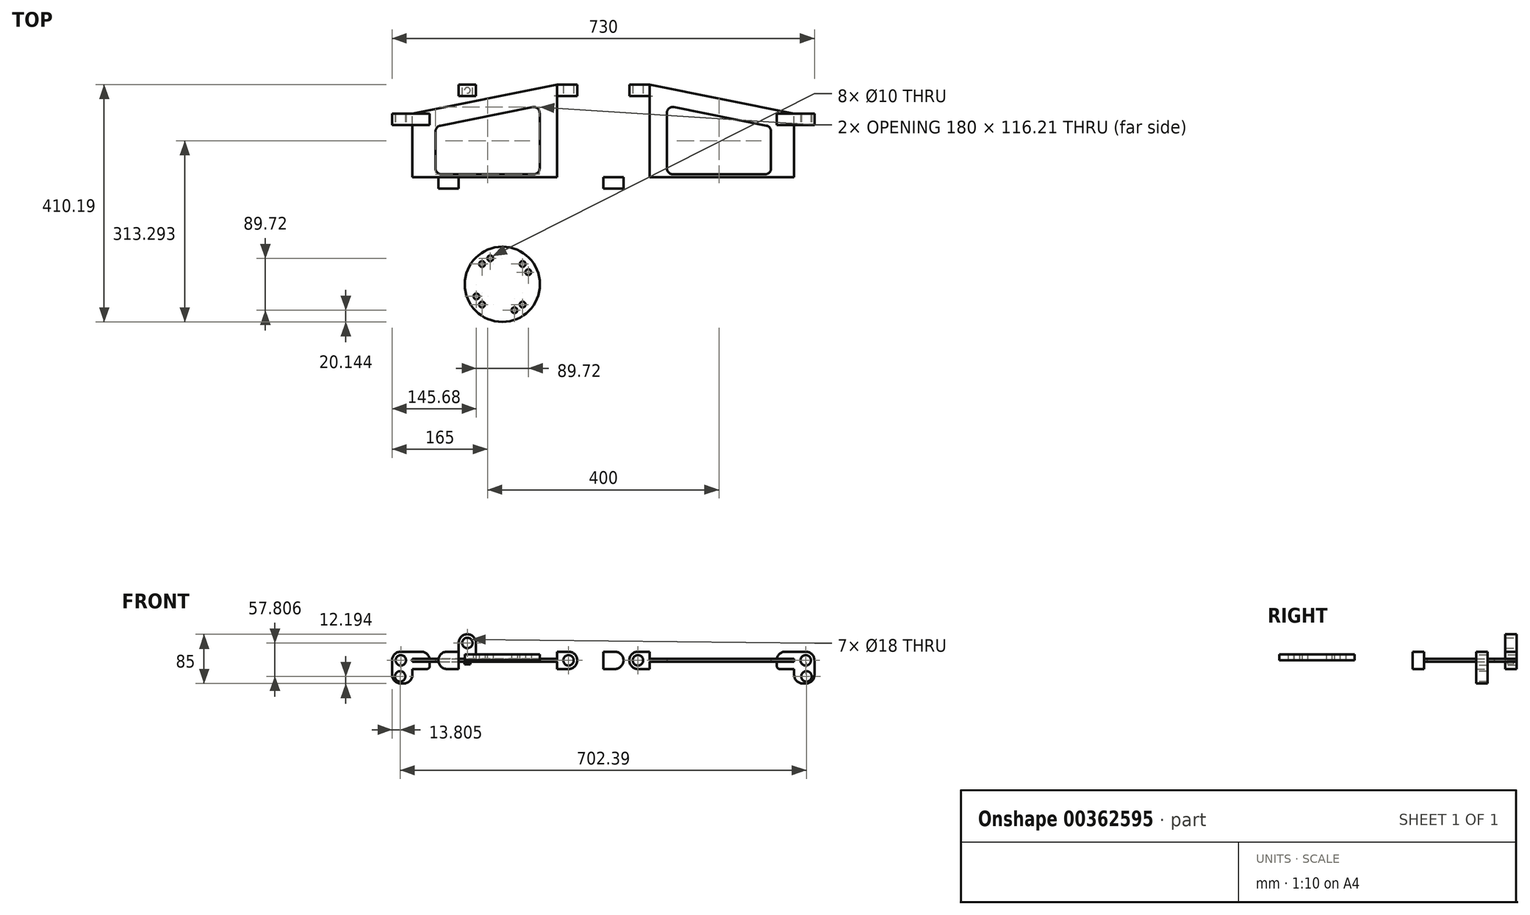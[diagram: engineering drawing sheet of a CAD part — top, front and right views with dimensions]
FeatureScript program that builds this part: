
annotation { "Feature Type Name" : "Feature", "Feature Type Description" : "" }
export const myFeature = defineFeature(function(context is Context, id is Id, definition is map)
    precondition{}
    {
        {
            var Q0;
            Q0=qCreatedBy(makeId("Top.planeOp"),FACE);
            var sketch = newSketch(context, id + "F0", { "sketchPlane" : qUnion([Q0])});
            skLineSegment(sketch, "E0", {"start": v(0, 0) * mm, "end": v(-250, -50) * mm});
            skLineSegment(sketch, "E1", {"start": v(-250, -180) * mm, "end": v(0, -180) * mm});
            skLineSegment(sketch, "E2", {"start": v(0, -180) * mm, "end": v(0, 0) * mm});
            skLineSegment(sketch, "E3", {"start": v(-30, -48.8) * mm, "end": v(-30, -145) * mm});
            skLineSegment(sketch, "E4", {"start": v(-201.96, -70.99) * mm, "end": v(-41.96, -38.99) * mm});
            skLineSegment(sketch, "E5", {"start": v(-200, -155) * mm, "end": v(-40, -155) * mm});
            skPoint(sketch, "E6.visualSharp", {"position": v(-30, -36.6) * mm});
            skArc(sketch, "E6.filletArc", {"start": v(-30, -48.8) * mm, "mid": v(-33.66, -41.06) * mm, "end": v(-41.96, -38.99) * mm});
            skPoint(sketch, "E7.visualSharp", {"position": v(-30, -155) * mm});
            skArc(sketch, "E8.filletArc", {"start": v(-40, -155) * mm, "mid": v(-32.93, -152.07) * mm, "end": v(-30, -145) * mm});
            skLineSegment(sketch, "E9", {"start": v(-250, -180) * mm, "end": v(-250, -50) * mm});
            skLineSegment(sketch, "E10", {"start": v(-210, -80.8) * mm, "end": v(-210, -145) * mm});
            skPoint(sketch, "E11.visualSharp", {"position": v(-210, -72.6) * mm});
            skArc(sketch, "E11.filletArc", {"start": v(-201.96, -70.99) * mm, "mid": v(-207.73, -74.45) * mm, "end": v(-210, -80.8) * mm});
            skLineSegment(sketch, "E12.bottom", {"start": v(-285, -180) * mm, "end": v(0, -180) * mm});
            skLineSegment(sketch, "E12.top", {"start": v(-285, -160) * mm, "end": v(0, -160) * mm});
            skLineSegment(sketch, "E12.left", {"start": v(-285, -180) * mm, "end": v(-285, -160) * mm});
            skLineSegment(sketch, "E12.right", {"start": v(0, -180) * mm, "end": v(0, -160) * mm});
            skLineSegment(sketch, "E13.bottom", {"start": v(-285, -50) * mm, "end": v(-220, -50) * mm});
            skLineSegment(sketch, "E13.top", {"start": v(-285, -70) * mm, "end": v(-220, -70) * mm});
            skLineSegment(sketch, "E13.left", {"start": v(-220, -50) * mm, "end": v(-220, -70) * mm});
            skLineSegment(sketch, "E13.right", {"start": v(-285, -50) * mm, "end": v(-285, -70) * mm});
            skPoint(sketch, "E14.visualSharp", {"position": v(-210, -155) * mm});
            skArc(sketch, "E14.filletArc", {"start": v(-210, -145) * mm, "mid": v(-207.07, -152.07) * mm, "end": v(-200, -155) * mm});
            skLineSegment(sketch, "E15.bottom", {"start": v(-250, 0) * mm, "end": v(-220, 0) * mm});
            skLineSegment(sketch, "E15.top", {"start": v(-250, -20) * mm, "end": v(-220, -20) * mm});
            skLineSegment(sketch, "E15.left", {"start": v(-250, 0) * mm, "end": v(-250, -20) * mm});
            skLineSegment(sketch, "E15.right", {"start": v(-220, 0) * mm, "end": v(-220, -20) * mm});
            skCircle(sketch, "E16", {"center": v(-235, -10) * mm, "radius": 5 * mm});
            skPoint(sketch, "E16.centerSnap0", {"position": v(-235, 0) * mm});
            skPoint(sketch, "E16.centerSnap1", {"position": v(-250, -10) * mm});
            skLineSegment(sketch, "E17.bottom", {"start": v(0, 0) * mm, "end": v(35, 0) * mm});
            skLineSegment(sketch, "E17.top", {"start": v(0, -20) * mm, "end": v(35, -20) * mm});
            skLineSegment(sketch, "E17.left", {"start": v(0, 0) * mm, "end": v(0, -20) * mm});
            skLineSegment(sketch, "E17.right", {"start": v(35, 0) * mm, "end": v(35, -20) * mm});
            skLineSegment(sketch, "E18.bottom", {"start": v(0, -180) * mm, "end": v(35, -180) * mm});
            skLineSegment(sketch, "E18.top", {"start": v(0, -160) * mm, "end": v(35, -160) * mm});
            skLineSegment(sketch, "E18.right", {"start": v(35, -180) * mm, "end": v(35, -160) * mm});
            skPoint(sketch, "E19.center", {"position": v(0, 0) * mm});
            skLineSegment(sketch, "E20.bottom", {"start": v(-129.6, -324.27) * mm, "end": v(-153.54, -390.05) * mm});
            skLineSegment(sketch, "E20.top", {"start": v(-195.38, -300.33) * mm, "end": v(-219.32, -366.1) * mm});
            skLineSegment(sketch, "E20.left", {"start": v(-129.6, -324.27) * mm, "end": v(-195.38, -300.33) * mm});
            skLineSegment(sketch, "E20.right", {"start": v(-153.54, -390.05) * mm, "end": v(-219.32, -366.1) * mm});
            skPoint(sketch, "E20.middle", {"position": v(-174.46, -345.19) * mm});
            skLineSegment(sketch, "E21.bottom", {"start": v(-139.46, -380.19) * mm, "end": v(-209.46, -380.19) * mm});
            skLineSegment(sketch, "E21.top", {"start": v(-139.46, -310.19) * mm, "end": v(-209.46, -310.19) * mm});
            skLineSegment(sketch, "E21.left", {"start": v(-139.46, -380.19) * mm, "end": v(-139.46, -310.19) * mm});
            skLineSegment(sketch, "E21.right", {"start": v(-209.46, -380.19) * mm, "end": v(-209.46, -310.19) * mm});
            skCircle(sketch, "E22", {"center": v(-174.46, -345.19) * mm, "radius": 65 * mm});
            skSolve(sketch);
        }
        {
            var Q0;
            {var subQ5=sQuery(id+"F0.wireOp",EDGE,"uvv03KWO-y48Y-yNLP-V4s5-E3iikQRzJ4Xf.right");Q0=makeQuery(id+"F0.imprint","IMPRINT",FACE,{"disambiguationData":[TD([[makeQuery(id+"F0.imprint","IMPRINT",EDGE,{"derivedFrom":subQ5}),1.0]])]});}
            var Q1;
            {var subQ0=sQuery(id+"F0.wireOp",EDGE,"1lGGe1Tg-SVZ4-Wade-i1KE-bgS1X0YdLzeq");var subQ1=makeQuery(id+"F0.imprint","INTERSECT",VERTEX,{"derivedFrom":[sQuery(id+"F0.wireOp",EDGE,"E0"),subQ0]});Q1=makeQuery(id+"F0.imprint","IMPRINT",FACE,{"disambiguationData":[TD([[makeQuery(id+"F0.imprint","IMPRINT",EDGE,{"disambiguationData":[TD([[subQ1,-1.0]])],"derivedFrom":subQ0}),1.0]])]});}
            var Q2;
            Q2=makeQuery(id+"F0.imprint","IMPRINT",FACE,{"disambiguationData":[TD([[makeQuery(id+"F0.imprint","IMPRINT",EDGE,{"derivedFrom":sQuery(id+"F0.wireOp",EDGE,"uvv03KWO-y48Y-yNLP-V4s5-E3iikQRzJ4Xf.bottom")}),-1.0]])]});
            var Q3;
            {var subQ0=sQuery(id+"F0.wireOp",EDGE,"uvv03KWO-y48Y-yNLP-V4s5-E3iikQRzJ4Xf.bottom");Q3=makeQuery(id+"F0.imprint","IMPRINT",FACE,{"disambiguationData":[TD([[makeQuery(id+"F0.imprint","IMPRINT",EDGE,{"derivedFrom":subQ0}),1.0]])]});}
            var Q4;
            Q4=makeQuery(id+"F0.imprint","IMPRINT",FACE,{"disambiguationData":[TD([[makeQuery(id+"F0.imprint","IMPRINT",EDGE,{"derivedFrom":sQuery(id+"F0.wireOp",EDGE,"0rv8Ym2q-hSoq-A4tP-6C1V-qJVH6aPOWYIx.bottom")}),1.0]])]});
            var Q5;
            Q5=makeQuery(id+"F0.imprint","IMPRINT",FACE,{"disambiguationData":[TD([[makeQuery(id+"F0.imprint","IMPRINT",EDGE,{"derivedFrom":sQuery(id+"F0.wireOp",EDGE,"E13.bottom")}),-1.0]])]});
            var Q6;
            Q6=makeQuery(id+"F0.imprint","IMPRINT",FACE,{"disambiguationData":[TD([[makeQuery(id+"F0.imprint","IMPRINT",EDGE,{"derivedFrom":sQuery(id+"F0.wireOp",EDGE,"E12.bottom")}),1.0]])]});
            var Q7;
            Q7=makeQuery(id+"F0.imprint","IMPRINT",FACE,{"disambiguationData":[TD([[makeQuery(id+"F0.imprint","IMPRINT",EDGE,{"derivedFrom":sQuery(id+"F0.wireOp",EDGE,"E0")}),1.0]])]});
            extrude(context, id + "F1", {"entities" : qUnion([Q0, Q1, Q2, Q3, Q4, Q5, Q6, Q7]), "endBound" : BoundingType.SYMMETRIC, "depth" : 5 * mm});
        }
        {
            var Q0;
            Q0=makeQuery(id+"F0.imprint","IMPRINT",FACE,{"disambiguationData":[TD([[makeQuery(id+"F0.imprint","IMPRINT",EDGE,{"derivedFrom":sQuery(id+"F0.wireOp",EDGE,"uvv03KWO-y48Y-yNLP-V4s5-E3iikQRzJ4Xf.bottom")}),-1.0]])]});
            var Q1;
            Q1=makeQuery(id+"F0.imprint","IMPRINT",FACE,{"disambiguationData":[TD([[makeQuery(id+"F0.imprint","IMPRINT",EDGE,{"derivedFrom":sQuery(id+"F0.wireOp",EDGE,"0rv8Ym2q-hSoq-A4tP-6C1V-qJVH6aPOWYIx.bottom")}),1.0]])]});
            var Q2;
            Q2=makeQuery(id+"F0.imprint","IMPRINT",FACE,{"disambiguationData":[TD([[makeQuery(id+"F0.imprint","IMPRINT",EDGE,{"derivedFrom":sQuery(id+"F0.wireOp",EDGE,"E17.bottom")}),-1.0]])]});
            var Q3;
            Q3=makeQuery(id+"F0.imprint","IMPRINT",FACE,{"disambiguationData":[TD([[makeQuery(id+"F0.imprint","IMPRINT",EDGE,{"derivedFrom":sQuery(id+"F0.wireOp",EDGE,"E18.bottom")}),1.0]])]});
            extrude(context, id + "F2", {"entities" : qUnion([Q0, Q1, Q2, Q3]), "operationType" : NewBodyOperationType.ADD, "endBound" : BoundingType.SYMMETRIC, "depth" : 30 * mm});
        }
        {
            var Q0;
            Q0=makeQuery(id+"F2.opExtrude","CAP_EDGE",EDGE,{"disambiguationData":[OSD([sQuery(id+"F0.wireOp",EDGE,"E18.right")])],"isStart":false});
            var Q1;
            Q1=makeQuery(id+"F2.opExtrude","CAP_EDGE",EDGE,{"disambiguationData":[OSD([sQuery(id+"F0.wireOp",EDGE,"E18.right")])],"isStart":true});
            var Q2;
            Q2=makeQuery(id+"F2.opExtrude","CAP_EDGE",EDGE,{"disambiguationData":[OSD([sQuery(id+"F0.wireOp",EDGE,"E17.right")])],"isStart":true});
            var Q3;
            Q3=makeQuery(id+"F2.opExtrude","CAP_EDGE",EDGE,{"disambiguationData":[OSD([sQuery(id+"F0.wireOp",EDGE,"E17.right")])],"isStart":false});
            fillet(context, id + "F3", {"entities" : qUnion([Q0, Q1, Q2, Q3]), "radius" : 15 * mm, "tangentPropagation" : true, "allowEdgeOverflow" : false});
        }
        {
            var Q0;
            Q0=makeQuery(id+"F0.imprint","IMPRINT",FACE,{"disambiguationData":[TD([[makeQuery(id+"F0.imprint","IMPRINT",EDGE,{"derivedFrom":sQuery(id+"F0.wireOp",EDGE,"E13.bottom")}),-1.0]])]});
            var Q1;
            Q1=makeQuery(id+"F0.imprint","IMPRINT",FACE,{"disambiguationData":[TD([[makeQuery(id+"F0.imprint","IMPRINT",EDGE,{"derivedFrom":sQuery(id+"F0.wireOp",EDGE,"E12.bottom")}),1.0]])]});
            extrude(context, id + "F4", {"entities" : qUnion([Q0, Q1]), "operationType" : NewBodyOperationType.ADD, "endBound" : BoundingType.SYMMETRIC, "depth" : 30 * mm});
        }
        {
            var Q0;
            Q0=makeQuery(id+"F4.opExtrude","CAP_EDGE",EDGE,{"disambiguationData":[OSD([sQuery(id+"F0.wireOp",EDGE,"E13.left")])],"isStart":false});
            var Q1;
            Q1=makeQuery(id+"F4.opExtrude","CAP_EDGE",EDGE,{"disambiguationData":[OSD([sQuery(id+"F0.wireOp",EDGE,"E13.right")])],"isStart":false});
            var Q2;
            Q2=makeQuery(id+"F4.opExtrude","CAP_EDGE",EDGE,{"disambiguationData":[OSD([sQuery(id+"F0.wireOp",EDGE,"E12.left")])],"isStart":false});
            var Q3;
            Q3=makeQuery(id+"F4.opExtrude","CAP_EDGE",EDGE,{"disambiguationData":[OSD([sQuery(id+"F0.wireOp",EDGE,"E12.right")])],"isStart":false});
            fillet(context, id + "F5", {"entities" : qUnion([Q0, Q1, Q2, Q3]), "radius" : 15 * mm, "tangentPropagation" : true, "allowEdgeOverflow" : false});
        }
        {
            var Q0;
            {var subQ5=sQuery(id+"F0.wireOp",EDGE,"E13.right");Q0=makeQuery(id+"F0.imprint","IMPRINT",FACE,{"disambiguationData":[TD([[makeQuery(id+"F0.imprint","IMPRINT",EDGE,{"derivedFrom":subQ5}),1.0]])]});}
            extrude(context, id + "F6", {"entities" : qUnion([Q0]), "operationType" : NewBodyOperationType.ADD, "oppositeDirection" : true, "depth" : 40 * mm});
        }
        {
            var Q0;
            Q0=makeQuery(id+"F6.opExtrude","CAP_EDGE",EDGE,{"disambiguationData":[OSD([sQuery(id+"F0.wireOp",EDGE,"E12.left")])],"isStart":false});
            var Q1;
            Q1=makeQuery(id+"F6.opExtrude","CAP_EDGE",EDGE,{"disambiguationData":[OSD([sQuery(id+"F0.wireOp",EDGE,"E12.right")])],"isStart":false});
            var Q2;
            Q2=makeQuery(id+"F4.opExtrude","CAP_EDGE",EDGE,{"disambiguationData":[OSD([sQuery(id+"F0.wireOp",EDGE,"E13.right")])],"isStart":true});
            var Q3;
            Q3=makeQuery(id+"F6.opExtrude","CAP_EDGE",EDGE,{"disambiguationData":[OSD([sQuery(id+"F0.wireOp",EDGE,"E9")])],"isStart":false});
            var Q4;
            Q4=makeQuery(id+"F6.opExtrude","CAP_EDGE",EDGE,{"disambiguationData":[OSD([sQuery(id+"F0.wireOp",EDGE,"E13.right")])],"isStart":false});
            var Q5;
            Q5=makeQuery(id+"F4.opExtrude","CAP_EDGE",EDGE,{"disambiguationData":[OSD([sQuery(id+"F0.wireOp",EDGE,"E12.left")])],"isStart":true});
            fillet(context, id + "F7", {"entities" : qUnion([Q0, Q1, Q2, Q3, Q4, Q5]), "radius" : 15 * mm, "tangentPropagation" : true, "allowEdgeOverflow" : false});
        }
        {
            var Q0;
            {var subQ0=sQuery(id+"F0.wireOp",EDGE,"E12.bottom");var subQ1=sQuery(id+"F0.wireOp",EDGE,"0rv8Ym2q-hSoq-A4tP-6C1V-qJVH6aPOWYIx.top");Q0=makeQuery(id+"F4.boolean.opBoolean","MERGE",FACE,{"derivedFrom":[makeQuery(id+"F2.boolean.opBoolean","MERGE",FACE,{"derivedFrom":[makeQuery(id+"F1.opExtrude","SWEPT_FACE",FACE,{"disambiguationData":[OSD([sQuery(id+"F0.wireOp",EDGE,"E1"),subQ1,subQ0])]}),makeQuery(id+"F2.opExtrude","SWEPT_FACE",FACE,{"disambiguationData":[OSD([subQ1])]})]}),makeQuery(id+"F4.opExtrude","SWEPT_FACE",FACE,{"disambiguationData":[OSD([subQ0])]})]});}
            var sketch = newSketch(context, id + "F8", { "sketchPlane" : qUnion([Q0])});
            skPoint(sketch, "E23", {"position": v(-270, 0) * mm});
            skPoint(sketch, "E24", {"position": v(20, 0) * mm});
            skPoint(sketch, "E25", {"position": v(-271.2, -27.8) * mm});
            skSolve(sketch);
        }
        {
            var Q0;
            Q0=sQuery(id+"F8.wireOp",VERTEX,"E23");
            var Q1;
            Q1=sQuery(id+"F8.wireOp",VERTEX,"E25");
            var Q2;
            Q2=sQuery(id+"F8.wireOp",VERTEX,"E24");
            var Q3;
            Q3=makeQuery(id+"F1.opExtrude","SWEPT_BODY",BODY,{"disambiguationData":[OSD([sQuery(id+"F0.wireOp",EDGE,"E0"),sQuery(id+"F0.wireOp",EDGE,"E1"),sQuery(id+"F0.wireOp",EDGE,"E2"),sQuery(id+"F0.wireOp",EDGE,"uvv03KWO-y48Y-yNLP-V4s5-E3iikQRzJ4Xf.top"),sQuery(id+"F0.wireOp",EDGE,"uvv03KWO-y48Y-yNLP-V4s5-E3iikQRzJ4Xf.left"),sQuery(id+"F0.wireOp",EDGE,"0rv8Ym2q-hSoq-A4tP-6C1V-qJVH6aPOWYIx.top"),sQuery(id+"F0.wireOp",EDGE,"0rv8Ym2q-hSoq-A4tP-6C1V-qJVH6aPOWYIx.left"),sQuery(id+"F0.wireOp",EDGE,"E3"),sQuery(id+"F0.wireOp",EDGE,"E4"),sQuery(id+"F0.wireOp",EDGE,"E5"),sQuery(id+"F0.wireOp",EDGE,"E6.filletArc"),sQuery(id+"F0.wireOp",EDGE,"E8.filletArc"),sQuery(id+"F0.wireOp",EDGE,"E9"),sQuery(id+"F0.wireOp",EDGE,"E10"),sQuery(id+"F0.wireOp",EDGE,"E11.filletArc"),sQuery(id+"F0.wireOp",EDGE,"ed4627cc-2027-4385-b44c-b2d2488a9f8e.filletArc"),sQuery(id+"F0.wireOp",EDGE,"E12.bottom"),sQuery(id+"F0.wireOp",EDGE,"E12.left"),sQuery(id+"F0.wireOp",EDGE,"E13.left")])]});
            hole(context, id + "F9", {"style" : HoleStyle.SIMPLE, "endStyle" : HoleEndStyle.THROUGH, "holeDiameter" : 18 * mm, "isTappedThrough" : true, "tappedDepth" : 12 * mm, "tapClearance" : 3, "locations" : qUnion([Q0, Q1, Q2]), "scope" : qUnion([Q3])});
        }
        {
            var Q0;
            Q0=makeQuery(id+"F4.opExtrude","CAP_EDGE",EDGE,{"disambiguationData":[OSD([sQuery(id+"F0.wireOp",EDGE,"E13.left")])],"isStart":true});
            var Q1;
            Q1=makeQuery(id+"F2.opExtrude","CAP_EDGE",EDGE,{"disambiguationData":[OSD([sQuery(id+"F0.wireOp",EDGE,"E17.left")])],"isStart":false});
            var Q2;
            Q2=makeQuery(id+"F2.opExtrude","CAP_EDGE",EDGE,{"disambiguationData":[OSD([sQuery(id+"F0.wireOp",EDGE,"E17.left")])],"isStart":true});
            var Q3;
            {var subQ0=sQuery(id+"F0.wireOp",EDGE,"E12.right");var subQ1=sQuery(id+"F0.wireOp",EDGE,"E17.left");var subQ2=sQuery(id+"F0.wireOp",EDGE,"E2");Q3=makeQuery(id+"F2.boolean.opBoolean","SPLIT",EDGE,{"disambiguationData":[topologyDisambiguationEdgeConnected([makeQuery(id+"F2.opExtrude","SWEPT_FACE",FACE,{"disambiguationData":[OSD([subQ1])]})])],"derivedFrom":makeQuery(id+"F1.opExtrude","CAP_EDGE",EDGE,{"disambiguationData":[OSD([subQ2,subQ1,subQ0])],"isStart":true})});}
            var Q4;
            {var subQ0=sQuery(id+"F0.wireOp",EDGE,"E12.right");Q4=makeQuery(id+"F6.boolean.opBoolean","INTERSECT",EDGE,{"derivedFrom":[makeQuery(id+"F4.boolean.opBoolean","MERGE",FACE,{"derivedFrom":[makeQuery(id+"F2.opExtrude","CAP_FACE",FACE,{"disambiguationData":[OSD([sQuery(id+"F0.wireOp",EDGE,"E18.bottom"),sQuery(id+"F0.wireOp",EDGE,"E18.top"),subQ0,sQuery(id+"F0.wireOp",EDGE,"E18.right")])],"isStart":true}),makeQuery(id+"F4.opExtrude","CAP_FACE",FACE,{"disambiguationData":[OSD([sQuery(id+"F0.wireOp",EDGE,"E12.bottom"),sQuery(id+"F0.wireOp",EDGE,"E12.top"),sQuery(id+"F0.wireOp",EDGE,"E12.left"),subQ0])],"isStart":true})]}),makeQuery(id+"F6.opExtrude","SWEPT_FACE",FACE,{"disambiguationData":[OSD([sQuery(id+"F0.wireOp",EDGE,"E9")])]})]});}
            var Q5;
            {var subQ0=sQuery(id+"F0.wireOp",EDGE,"E12.right");var subQ1=sQuery(id+"F0.wireOp",EDGE,"E17.left");var subQ2=sQuery(id+"F0.wireOp",EDGE,"E2");Q5=makeQuery(id+"F2.boolean.opBoolean","SPLIT",EDGE,{"disambiguationData":[topologyDisambiguationEdgeConnected([makeQuery(id+"F2.opExtrude","SWEPT_FACE",FACE,{"disambiguationData":[OSD([subQ1])]})])],"derivedFrom":makeQuery(id+"F1.opExtrude","CAP_EDGE",EDGE,{"disambiguationData":[OSD([subQ2,subQ1,subQ0])],"isStart":false})});}
            fillet(context, id + "F10", {"entities" : qUnion([Q0, Q1, Q2, Q3, Q4, Q5]), "radius" : 5 * mm, "tangentPropagation" : true, "allowEdgeOverflow" : false});
        }
        {
            var Q0;
            Q0=makeQuery(id+"F1.opExtrude","CAP_EDGE",EDGE,{"disambiguationData":[OSD([sQuery(id+"F0.wireOp",EDGE,"E5")])],"isStart":false});
            cPoint(context, id + "F11", {"entities" : qUnion([Q0]), "parameter" : 0.5});
        }
        {
            var Q0;
            Q0=makeQuery(id+"F1.opExtrude","SWEPT_BODY",BODY,{"disambiguationData":[OSD([sQuery(id+"F0.wireOp",EDGE,"E0"),sQuery(id+"F0.wireOp",EDGE,"E1"),sQuery(id+"F0.wireOp",EDGE,"E2"),sQuery(id+"F0.wireOp",EDGE,"uvv03KWO-y48Y-yNLP-V4s5-E3iikQRzJ4Xf.top"),sQuery(id+"F0.wireOp",EDGE,"uvv03KWO-y48Y-yNLP-V4s5-E3iikQRzJ4Xf.left"),sQuery(id+"F0.wireOp",EDGE,"0rv8Ym2q-hSoq-A4tP-6C1V-qJVH6aPOWYIx.top"),sQuery(id+"F0.wireOp",EDGE,"0rv8Ym2q-hSoq-A4tP-6C1V-qJVH6aPOWYIx.left"),sQuery(id+"F0.wireOp",EDGE,"E3"),sQuery(id+"F0.wireOp",EDGE,"E4"),sQuery(id+"F0.wireOp",EDGE,"E5"),sQuery(id+"F0.wireOp",EDGE,"E6.filletArc"),sQuery(id+"F0.wireOp",EDGE,"E8.filletArc"),sQuery(id+"F0.wireOp",EDGE,"E9"),sQuery(id+"F0.wireOp",EDGE,"E10"),sQuery(id+"F0.wireOp",EDGE,"E11.filletArc"),sQuery(id+"F0.wireOp",EDGE,"E12.bottom"),sQuery(id+"F0.wireOp",EDGE,"E12.left"),sQuery(id+"F0.wireOp",EDGE,"E13.left"),sQuery(id+"F0.wireOp",EDGE,"E14.filletArc")])]});
            var Q1;
            Q1=makeQuery(id+"F1.opExtrude","CAP_VERTEX",VERTEX,{"disambiguationData":[OSD([sQuery(id+"F0.wireOp",EDGE,"E5"),sQuery(id+"F0.wireOp",EDGE,"E8.filletArc")])],"isStart":false});
            var Q2;
            Q2 = qCreatedBy(id + "F11" ,VERTEX);
            transform(context, id + "F12", {"entities" : qUnion([Q0]), "transformType" : TransformType.TRANSLATION_ENTITY, "oppositeDirectionEntity" : false, "transformLine" : qUnion([Q1, Q2]), "makeCopy" : false});
        }
        {
            var Q0;
            Q0=makeQuery(id+"F1.opExtrude","SWEPT_BODY",BODY,{"disambiguationData":[OSD([sQuery(id+"F0.wireOp",EDGE,"E0"),sQuery(id+"F0.wireOp",EDGE,"E1"),sQuery(id+"F0.wireOp",EDGE,"E2"),sQuery(id+"F0.wireOp",EDGE,"uvv03KWO-y48Y-yNLP-V4s5-E3iikQRzJ4Xf.top"),sQuery(id+"F0.wireOp",EDGE,"uvv03KWO-y48Y-yNLP-V4s5-E3iikQRzJ4Xf.left"),sQuery(id+"F0.wireOp",EDGE,"0rv8Ym2q-hSoq-A4tP-6C1V-qJVH6aPOWYIx.top"),sQuery(id+"F0.wireOp",EDGE,"0rv8Ym2q-hSoq-A4tP-6C1V-qJVH6aPOWYIx.left"),sQuery(id+"F0.wireOp",EDGE,"E3"),sQuery(id+"F0.wireOp",EDGE,"E4"),sQuery(id+"F0.wireOp",EDGE,"E5"),sQuery(id+"F0.wireOp",EDGE,"E6.filletArc"),sQuery(id+"F0.wireOp",EDGE,"E8.filletArc"),sQuery(id+"F0.wireOp",EDGE,"E9"),sQuery(id+"F0.wireOp",EDGE,"E10"),sQuery(id+"F0.wireOp",EDGE,"E11.filletArc"),sQuery(id+"F0.wireOp",EDGE,"E12.bottom"),sQuery(id+"F0.wireOp",EDGE,"E12.left"),sQuery(id+"F0.wireOp",EDGE,"E13.left"),sQuery(id+"F0.wireOp",EDGE,"E14.filletArc")])]});
            var Q1;
            Q1=qCreatedBy(makeId("Right.planeOp"),FACE);
            mirror(context, id + "F13", {"entities" : qUnion([Q0]), "mirrorPlane" : qUnion([Q1])});
        }
        {
            var Q0;
            Q0=makeQuery(id+"F0.imprint","IMPRINT",FACE,{"disambiguationData":[TD([[makeQuery(id+"F0.imprint","IMPRINT",EDGE,{"derivedFrom":sQuery(id+"F0.wireOp",EDGE,"E15.bottom")}),-1.0]])]});
            var Q1;
            Q1=makeQuery(id+"F0.imprint","IMPRINT",FACE,{"disambiguationData":[TD([[makeQuery(id+"F0.imprint","IMPRINT",EDGE,{"derivedFrom":sQuery(id+"F0.wireOp",EDGE,"E16")}),1.0]])]});
            extrude(context, id + "F14", {"entities" : qUnion([Q0, Q1]), "depth" : 45 * mm});
        }
        {
            var Q0;
            Q0=makeQuery(id+"F0.imprint","IMPRINT",FACE,{"disambiguationData":[TD([[makeQuery(id+"F0.imprint","IMPRINT",EDGE,{"derivedFrom":sQuery(id+"F0.wireOp",EDGE,"E16")}),1.0]])]});
            var Q1;
            Q1=sQuery(id+"F0.wireOp",EDGE,"E16");
            extrude(context, id + "F15", {"entities" : qUnion([Q0]), "operationType" : NewBodyOperationType.ADD, "surfaceEntities" : qUnion([Q1]), "oppositeDirection" : true, "depth" : 7 * mm});
        }
        {
            var Q0;
            Q0=makeQuery(id+"F14.opExtrude","CAP_EDGE",EDGE,{"disambiguationData":[OSD([sQuery(id+"F0.wireOp",EDGE,"E15.left")])],"isStart":false});
            var Q1;
            Q1=makeQuery(id+"F14.opExtrude","CAP_EDGE",EDGE,{"disambiguationData":[OSD([sQuery(id+"F0.wireOp",EDGE,"E15.right")])],"isStart":false});
            fillet(context, id + "F16", {"entities" : qUnion([Q0, Q1]), "radius" : 15 * mm, "tangentPropagation" : true, "allowEdgeOverflow" : false});
        }
        {
            var Q0;
            Q0=makeQuery(id+"F14.opExtrude","SWEPT_FACE",FACE,{"disambiguationData":[OSD([sQuery(id+"F0.wireOp",EDGE,"E15.bottom")])]});
            var sketch = newSketch(context, id + "F17", { "sketchPlane" : qUnion([Q0])});
            skPoint(sketch, "E26", {"position": v(235, 30) * mm});
            skSolve(sketch);
        }
        {
            var Q0;
            Q0=sQuery(id+"F17.wireOp",VERTEX,"E26");
            var Q1;
            Q1=makeQuery(id+"F14.opExtrude","SWEPT_BODY",BODY,{"disambiguationData":[OSD([sQuery(id+"F0.wireOp",EDGE,"E15.bottom"),sQuery(id+"F0.wireOp",EDGE,"E15.top"),sQuery(id+"F0.wireOp",EDGE,"E15.left"),sQuery(id+"F0.wireOp",EDGE,"E15.right")])]});
            hole(context, id + "F18", {"style" : HoleStyle.SIMPLE, "endStyle" : HoleEndStyle.THROUGH, "holeDiameter" : 18 * mm, "isTappedThrough" : true, "tappedDepth" : 12 * mm, "tapClearance" : 3, "locations" : qUnion([Q0]), "scope" : qUnion([Q1])});
        }
        {
            var Q0;
            Q0=makeQuery(id+"F0.imprint","IMPRINT",FACE,{"disambiguationData":[TD([[makeQuery(id+"F0.imprint","IMPRINT",EDGE,{"derivedFrom":sQuery(id+"F0.wireOp",EDGE,"E22")}),1.0]])]});
            var Q1;
            {var subQ0=sQuery(id+"F0.wireOp",EDGE,"E20.right");var subQ1=sQuery(id+"F0.wireOp",EDGE,"E20.bottom");var subQ2=makeQuery(id+"F0.imprint","INTERSECT",VERTEX,{"derivedFrom":[subQ1,subQ0]});Q1=makeQuery(id+"F0.imprint","IMPRINT",FACE,{"disambiguationData":[TD([[makeQuery(id+"F0.imprint","IMPRINT",EDGE,{"disambiguationData":[TD([[subQ2,1.0]])],"derivedFrom":subQ1}),-1.0]])]});}
            var Q2;
            {var subQ0=sQuery(id+"F0.wireOp",EDGE,"E20.right");var subQ1=sQuery(id+"F0.wireOp",EDGE,"E20.top");var subQ2=makeQuery(id+"F0.imprint","INTERSECT",VERTEX,{"derivedFrom":[subQ1,subQ0]});Q2=makeQuery(id+"F0.imprint","IMPRINT",FACE,{"disambiguationData":[TD([[makeQuery(id+"F0.imprint","IMPRINT",EDGE,{"disambiguationData":[TD([[subQ2,1.0]])],"derivedFrom":subQ1}),1.0]])]});}
            var Q3;
            {var subQ0=sQuery(id+"F0.wireOp",EDGE,"E21.top");var subQ1=sQuery(id+"F0.wireOp",EDGE,"E20.top");var subQ2=makeQuery(id+"F0.imprint","INTERSECT",VERTEX,{"derivedFrom":[subQ1,subQ0]});Q3=makeQuery(id+"F0.imprint","IMPRINT",FACE,{"disambiguationData":[TD([[makeQuery(id+"F0.imprint","IMPRINT",EDGE,{"disambiguationData":[TD([[subQ2,-1.0]])],"derivedFrom":subQ1}),-1.0]])]});}
            var Q4;
            {var subQ0=sQuery(id+"F0.wireOp",EDGE,"E21.bottom");var subQ1=sQuery(id+"F0.wireOp",EDGE,"E20.right");var subQ2=makeQuery(id+"F0.imprint","INTERSECT",VERTEX,{"derivedFrom":[subQ1,subQ0]});Q4=makeQuery(id+"F0.imprint","IMPRINT",FACE,{"disambiguationData":[TD([[makeQuery(id+"F0.imprint","IMPRINT",EDGE,{"disambiguationData":[TD([[subQ2,-1.0]])],"derivedFrom":subQ1}),1.0]])]});}
            var Q5;
            {var subQ5=sQuery(id+"F0.wireOp",EDGE,"E21.left");var subQ13=sQuery(id+"F0.wireOp",EDGE,"E20.bottom");var subQ14=makeQuery(id+"F0.imprint","INTERSECT",VERTEX,{"derivedFrom":[subQ13,subQ5]});Q5=makeQuery(id+"F0.imprint","IMPRINT",FACE,{"disambiguationData":[TD([[makeQuery(id+"F0.imprint","IMPRINT",EDGE,{"disambiguationData":[TD([[subQ14,-1.0]])],"derivedFrom":subQ13}),-1.0]])]});}
            var Q6;
            {var subQ0=sQuery(id+"F0.wireOp",EDGE,"E20.left");var subQ1=sQuery(id+"F0.wireOp",EDGE,"E20.top");var subQ2=makeQuery(id+"F0.imprint","INTERSECT",VERTEX,{"derivedFrom":[subQ1,subQ0]});Q6=makeQuery(id+"F0.imprint","IMPRINT",FACE,{"disambiguationData":[TD([[makeQuery(id+"F0.imprint","IMPRINT",EDGE,{"disambiguationData":[TD([[subQ2,-1.0]])],"derivedFrom":subQ1}),1.0]])]});}
            var Q7;
            {var subQ0=sQuery(id+"F0.wireOp",EDGE,"E21.left");var subQ1=sQuery(id+"F0.wireOp",EDGE,"E20.left");var subQ2=makeQuery(id+"F0.imprint","INTERSECT",VERTEX,{"derivedFrom":[subQ1,subQ0]});Q7=makeQuery(id+"F0.imprint","IMPRINT",FACE,{"disambiguationData":[TD([[makeQuery(id+"F0.imprint","IMPRINT",EDGE,{"disambiguationData":[TD([[subQ2,-1.0]])],"derivedFrom":subQ1}),-1.0]])]});}
            var Q8;
            {var subQ0=sQuery(id+"F0.wireOp",EDGE,"E20.left");var subQ1=sQuery(id+"F0.wireOp",EDGE,"E20.bottom");var subQ2=makeQuery(id+"F0.imprint","INTERSECT",VERTEX,{"derivedFrom":[subQ1,subQ0]});Q8=makeQuery(id+"F0.imprint","IMPRINT",FACE,{"disambiguationData":[TD([[makeQuery(id+"F0.imprint","IMPRINT",EDGE,{"disambiguationData":[TD([[subQ2,-1.0]])],"derivedFrom":subQ1}),-1.0]])]});}
            var Q9;
            {var subQ0=sQuery(id+"F0.wireOp",EDGE,"E21.left");var subQ1=sQuery(id+"F0.wireOp",EDGE,"E20.bottom");var subQ2=makeQuery(id+"F0.imprint","INTERSECT",VERTEX,{"derivedFrom":[subQ1,subQ0]});Q9=makeQuery(id+"F0.imprint","IMPRINT",FACE,{"disambiguationData":[TD([[makeQuery(id+"F0.imprint","IMPRINT",EDGE,{"disambiguationData":[TD([[subQ2,-1.0]])],"derivedFrom":subQ1}),1.0]])]});}
            extrude(context, id + "F19", {"entities" : qUnion([Q0, Q1, Q2, Q3, Q4, Q5, Q6, Q7, Q8, Q9]), "depth" : 10 * mm});
        }
        {
            var Q0;
            Q0=sQuery(id+"F0.wireOp",VERTEX,"E21.right.end");
            var Q1;
            Q1=sQuery(id+"F0.wireOp",VERTEX,"E20.right.end");
            var Q2;
            Q2=sQuery(id+"F0.wireOp",VERTEX,"E21.right.start");
            var Q3;
            Q3=sQuery(id+"F0.wireOp",VERTEX,"E20.bottom.end");
            var Q4;
            Q4=sQuery(id+"F0.wireOp",VERTEX,"E21.left.start");
            var Q5;
            Q5=sQuery(id+"F0.wireOp",VERTEX,"E20.bottom.start");
            var Q6;
            Q6=sQuery(id+"F0.wireOp",VERTEX,"E21.left.end");
            var Q7;
            Q7=sQuery(id+"F0.wireOp",VERTEX,"E20.top.start");
            var Q8;
            Q8=makeQuery(id+"F19.opExtrude","SWEPT_BODY",BODY,{"disambiguationData":[OSD([sQuery(id+"F0.wireOp",EDGE,"E22")])]});
            hole(context, id + "F20", {"style" : HoleStyle.SIMPLE, "endStyle" : HoleEndStyle.THROUGH, "oppositeDirection" : true, "holeDiameter" : 10 * mm, "isTappedThrough" : true, "tappedDepth" : 12 * mm, "tapClearance" : 3, "startFromSketch" : true, "locations" : qUnion([Q0, Q1, Q2, Q3, Q4, Q5, Q6, Q7]), "scope" : qUnion([Q8])});
        }
    });
